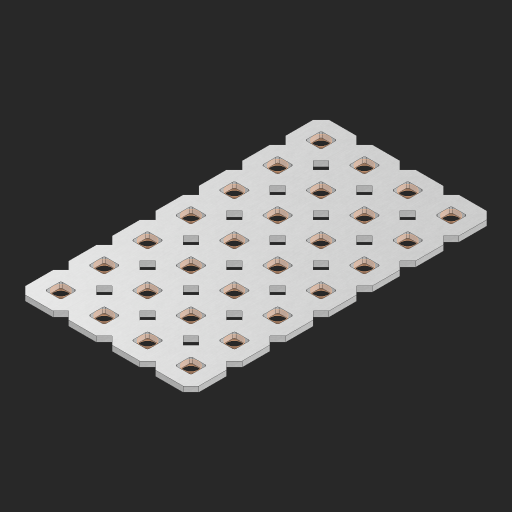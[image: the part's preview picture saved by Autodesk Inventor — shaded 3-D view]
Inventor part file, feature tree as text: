
AUTODESK INVENTOR PART (.ipt)
format: ipt  version: 2023 (Build 270158000, 158)  size: 622,592 bytes
history: native  units: in
note: dims shown in document units (in); Inventor stores cm internally (conversion verified against a paired STEP export)
features: other x29, extrude x27, sketch x2, pattern_linear x1
ambient origin geometry x8: Origin, YZ Plane, XZ Plane, XY Plane, X Axis, Y Axis, Z Axis, Center Point
bodies: Solid1 (feature_tree), Body (feature_tree)
feature tree (59):
  pattern_linear  "Rectangular Pattern1"  Spacing1=0.09in  [1 undecoded]
  sketch  "Sketch1"  dims[d1=0.5in]
  sketch  "Sketch2"  dims[d2=0.182in d3=0.09in d4=0.09in d5=0.09in d6=0.09in d7=0.09in d8=0.09in d9=0.09in d10=0.09in d11=0.02in d13=0.0in d14=0.172in d15=0.0625in d16=0.0in d19=0.5in d22=0.5in]
  other  "Srf1"
  other  "Srf126"
  other  "Srf127"
  other  "Srf128"
  other  "Srf129"
  other  "Srf130"
  other  "Srf131"
  other  "Srf268"
  other  "Srf269"
  other  "Srf270"
  other  "Srf271"
  other  "Srf272"
  other  "Srf273"
  other  "Srf274"
  other  "Srf293"
  other  "Srf294"
  other  "Srf295"
  other  "Srf296"
  other  "Srf297"
  other  "Srf298"
  other  "Srf299"
  other  "Srf318"
  other  "Srf319"
  other  "Srf320"
  other  "Srf321"
  other  "Srf322"
  other  "Srf323"
  other  "Srf324"
  other  "Circle"
  extrude  "ExtrusionSrf126"  Depth=0.09in
  extrude  "ExtrusionSrf127"  Depth=0.09in
  extrude  "ExtrusionSrf128"  Depth=0.09in
  extrude  "ExtrusionSrf129"  Depth=0.09in
  extrude  "ExtrusionSrf130"  Depth=0.09in
  extrude  "ExtrusionSrf131"  Depth=0.09in
  extrude  "ExtrusionSrf268"  Depth=0.09in
  extrude  "ExtrusionSrf269"  Depth=0.02in
  extrude  "ExtrusionSrf270"  TaperAngle=0.0deg  [1 undecoded]
  extrude  "ExtrusionSrf271"  Depth=0.5in
  extrude  "ExtrusionSrf272"  Depth=0.0625in TaperAngle=0.0deg
  extrude  "ExtrusionSrf273"  Depth=0.5in
  extrude  "ExtrusionSrf274"  Depth=0.5in
  extrude  "ExtrusionSrf293"  [1 undecoded]
  extrude  "ExtrusionSrf294"  [1 undecoded]
  extrude  "ExtrusionSrf295"  [1 undecoded]
  extrude  "ExtrusionSrf296"  [1 undecoded]
  extrude  "ExtrusionSrf297"  [1 undecoded]
  extrude  "ExtrusionSrf298"  [1 undecoded]
  extrude  "ExtrusionSrf299"  [1 undecoded]
  extrude  "ExtrusionSrf318"  [1 undecoded]
  extrude  "ExtrusionSrf319"  [1 undecoded]
  extrude  "ExtrusionSrf320"  [1 undecoded]
  extrude  "ExtrusionSrf321"  [1 undecoded]
  extrude  "ExtrusionSrf322"  [1 undecoded]
  extrude  "ExtrusionSrf323"  [1 undecoded]
  extrude  "ExtrusionSrf324"  [1 undecoded]
note: 16 required parameter values undecoded (feature->parameter linkage not recoverable at this tier; creation-order binding heuristic only, values carry confidence <= 0.55)
